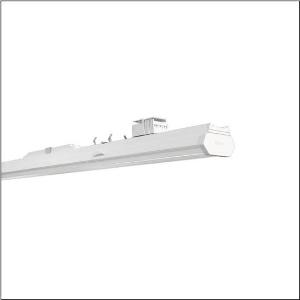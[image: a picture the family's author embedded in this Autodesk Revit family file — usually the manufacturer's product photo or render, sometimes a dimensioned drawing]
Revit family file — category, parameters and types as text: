
# Revit family: licross_r__11_protected_ho_51td12dn4fxm3c_9ee7
name_source: partatom
category: Lighting Fixtures
units: mm (PartAtom-declared; Revit-internal decimal feet)

## family parameters
Cut with Voids When Loaded = No
Host = Face
Light Source = No
Part Type = Normal
Room Calculation Point = No
Round Connector Dimension = Use Diameter
Shared = No

## types (1)
- --- (1 x LED, 970 lm, 7.4 W, 4000K)
    Apparent Load = 7 VA
    CIE Flux Codes = 70 91 97 98 100
    Color Rendering = 80
    Color Temperature = 4000K
    Default Elevation = 1800 mm
    Description = Licross® 11 Protected HO, luminaire insert, of sheet steel, galvanised, coil coated, white, length: 1.500mm, width: 90mm, height: 101mm, LED rated luminous flux: 15.270lm, light colour: 840, control gear: DALI 2 (for two DALI lines), with plug, 6-pole, with phase selection, for trunking rail, 14-core, mains connection: 220..240V, AC, 50/60Hz, rated input power: 91W, for trunking rail, 14-core, halogen-free wiring, for emergency light function, converter,control gear: single battery element, battery: LiFePO4, 9Ah, primary light control with lens, of plastic, primary optical cover: cover, of PMMA, light emission: direct distribution, primary light characteristic: symmetric, protection rating (complete): IP54, insulation class (complete): insulation class I (protective earthing), certification: CE, UKCA, protection symbol: D if used in an environment with non-conductive dust loads with corresponding accessories, impact resistance: IK06, permissible ambient temperature for indoor applications: +5..+30°C, standard: EN 60598-2-22, LABS conformity tested according to VDMA 24364:2018-05, reducing of maximum allowable ambient temperature of 5°C with ceiling mounting, corresponds to IFS (International Featured Standards) requirements for safety and quality in the food industry, packaging unit: 1 piece
    Height = 92 mm
    Lamp = 1 x LED
    Lamp Light Flux = 970 lm
    Lamp Power = 7.4 W
    Lamp count = 1
    Length = 1500 mm
    Luminous efficacy = 131 lm/W
    Manufacturer = Siteco
    ModVariant = No
    Model = 51TD12DN4FXM3C
    Mounting Place = Ceiling
    Mounting Type = Pendant
    Number of Poles = 1
    OnlyDefault = Yes
    Power Factor = 1
    Product Name = Licross® 11 Protected HO
    Product group = luminaire insert
    ProductGroupID = 901
    Protection Class = Protection class I
    Protection Degree = IP 54
    RLX_Detail_Level = 1
    RLX_Emergency_Light_Flux = 0 lm
    RLX_Emergency_Type = 0
    RLX_Emergency_Type_DB = No
    RlxData = <blob elided: 24901 chars, md5=48d1a298>
    Socket = socket
    Standby Power = 0 W
    System Light Flux = 970 lm
    System Power = 7 W
    Type Comments = : emergency light operation: 3 h
    Type Image = l_1256145.jpg
    URL = http://relux.com
    VarID = @adj_059709
    Voltage = 0 V
    Weight = 0.00 kg
    Width = 88 mm

## geometry (parser evidence)
native form markers: Blend x4, Sweep x10
no freeform markers — native parametric forms only
